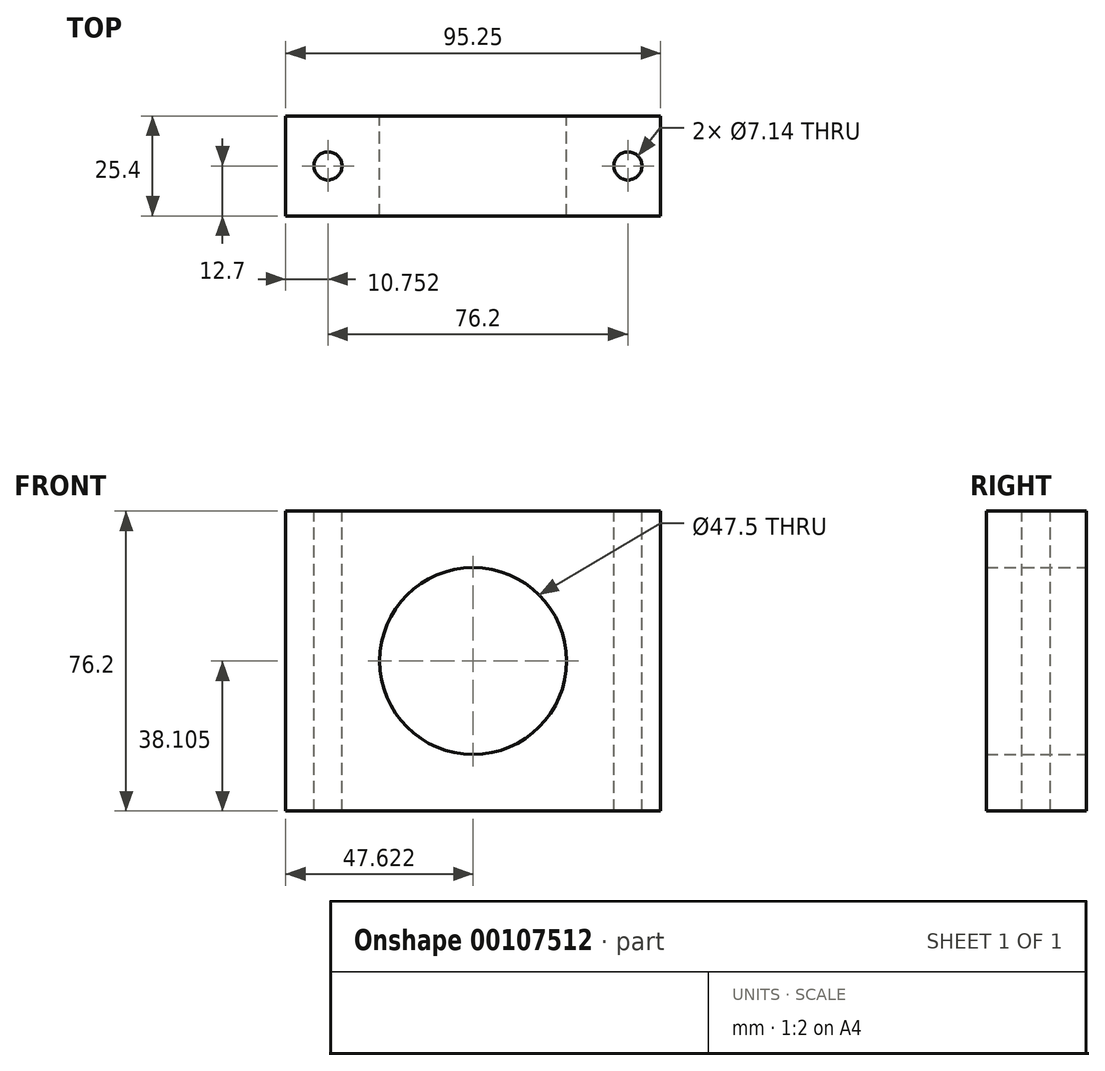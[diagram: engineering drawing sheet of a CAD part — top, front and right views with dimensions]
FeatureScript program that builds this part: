
annotation { "Feature Type Name" : "Feature", "Feature Type Description" : "" }
export const myFeature = defineFeature(function(context is Context, id is Id, definition is map)
    precondition{}
    {
        {
            var Q0;
            Q0=qCreatedBy(makeId("Front.planeOp"),FACE);
            var sketch = newSketch(context, id + "F0", { "sketchPlane" : qUnion([Q0])});
            skLineSegment(sketch, "E0.bottom", {"start": v(-40.36, 45.52) * mm, "end": v(54.89, 45.52) * mm});
            skLineSegment(sketch, "E0.top", {"start": v(-40.36, -30.68) * mm, "end": v(54.89, -30.68) * mm});
            skLineSegment(sketch, "E0.left", {"start": v(-40.36, 45.52) * mm, "end": v(-40.36, -30.68) * mm});
            skLineSegment(sketch, "E0.right", {"start": v(54.89, 45.52) * mm, "end": v(54.89, -30.68) * mm});
            skLineSegment(sketch, "E1", {"start": v(-40.36, 7.42) * mm, "end": v(54.89, 7.42) * mm, "construction": true});
            skLineSegment(sketch, "E2", {"start": v(7.26, 45.52) * mm, "end": v(7.26, -30.68) * mm, "construction": true});
            skCircle(sketch, "E3", {"center": v(7.26, 7.42) * mm, "radius": 23.75 * mm});
            skSolve(sketch);
        }
        {
            var Q0;
            Q0=makeQuery(id+"F0.imprint","IMPRINT",FACE,{"disambiguationData":[TD([[makeQuery(id+"F0.imprint","IMPRINT",EDGE,{"derivedFrom":sQuery(id+"F0.wireOp",EDGE,"E0.bottom")}),-1.0]])]});
            extrude(context, id + "F1", {"entities" : qUnion([Q0]), "depth" : 25.4 * mm});
        }
        {
            var Q0;
            Q0=makeQuery(id+"F1.opExtrude","SWEPT_FACE",FACE,{"disambiguationData":[OSD([sQuery(id+"F0.wireOp",EDGE,"E0.bottom")])]});
            var sketch = newSketch(context, id + "F2", { "sketchPlane" : qUnion([Q0])});
            skCircle(sketch, "E4", {"center": v(-29.6, -12.7) * mm, "radius": 3.57 * mm});
            skPoint(sketch, "E4.centerSnap0", {"position": v(-40.36, -12.7) * mm});
            skCircle(sketch, "E5", {"center": v(46.6, -12.7) * mm, "radius": 3.57 * mm});
            skSolve(sketch);
        }
        {
            var Q0;
            Q0 = qSketchRegion(id + "F2", true);
            extrude(context, id + "F3", {"entities" : qUnion([Q0]), "operationType" : NewBodyOperationType.REMOVE, "oppositeDirection" : true, "depth" : 76.2 * mm});
        }
    });
